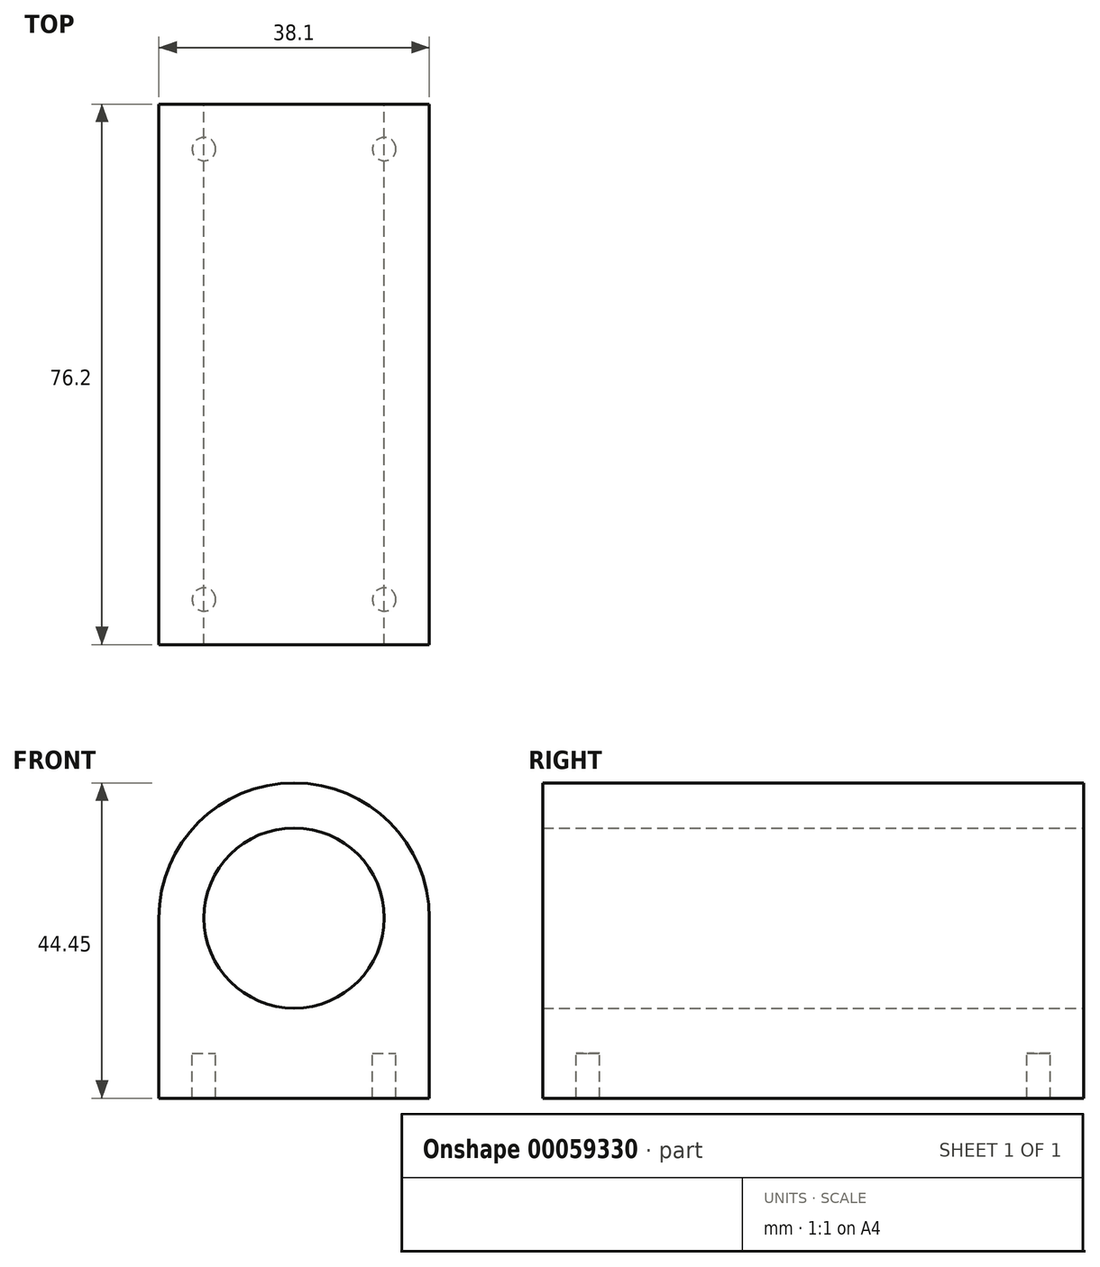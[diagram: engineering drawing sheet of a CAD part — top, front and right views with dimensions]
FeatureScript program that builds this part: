
annotation { "Feature Type Name" : "Feature", "Feature Type Description" : "" }
export const myFeature = defineFeature(function(context is Context, id is Id, definition is map)
    precondition{}
    {
        {
            var Q0;
            Q0=qCreatedBy(makeId("Front.planeOp"),FACE);
            var sketch = newSketch(context, id + "F0", { "sketchPlane" : qUnion([Q0])});
            skCircle(sketch, "E0", {"center": v(0, 0) * mm, "radius": 12.7 * mm});
            skArc(sketch, "E1", {"start": v(19.05, 0) * mm, "mid": v(0, 19.05) * mm, "end": v(-19.05, 0) * mm});
            skLineSegment(sketch, "E2", {"start": v(-19.05, 0) * mm, "end": v(-19.05, -25.4) * mm});
            skLineSegment(sketch, "E3", {"start": v(19.05, 0) * mm, "end": v(19.05, -25.4) * mm});
            skLineSegment(sketch, "E4", {"start": v(19.05, -25.4) * mm, "end": v(-19.05, -25.4) * mm});
            skSolve(sketch);
        }
        {
            var Q0;
            Q0 = qSketchRegion(id + "F0", true);
            extrude(context, id + "F1", {"entities" : qUnion([Q0]), "depth" : 76.2 * mm});
        }
        {
            var Q0;
            Q0=makeQuery(id+"F1.opExtrude","SWEPT_FACE",FACE,{"disambiguationData":[OSD([sQuery(id+"F0.wireOp",EDGE,"E4")])]});
            var sketch = newSketch(context, id + "F2", { "sketchPlane" : qUnion([Q0])});
            skCircle(sketch, "E5", {"center": v(-12.7, 69.85) * mm, "radius": 1.65 * mm});
            skCircle(sketch, "E6", {"center": v(12.7, 69.85) * mm, "radius": 1.65 * mm});
            skCircle(sketch, "E7", {"center": v(-12.7, 6.35) * mm, "radius": 1.65 * mm});
            skCircle(sketch, "E8", {"center": v(12.7, 6.35) * mm, "radius": 1.65 * mm});
            skSolve(sketch);
        }
        {
            var Q0;
            Q0 = qSketchRegion(id + "F2", true);
            extrude(context, id + "F3", {"entities" : qUnion([Q0]), "operationType" : NewBodyOperationType.REMOVE, "endBound" : BoundingType.SYMMETRIC, "depth" : 12.7 * mm});
        }
    });
